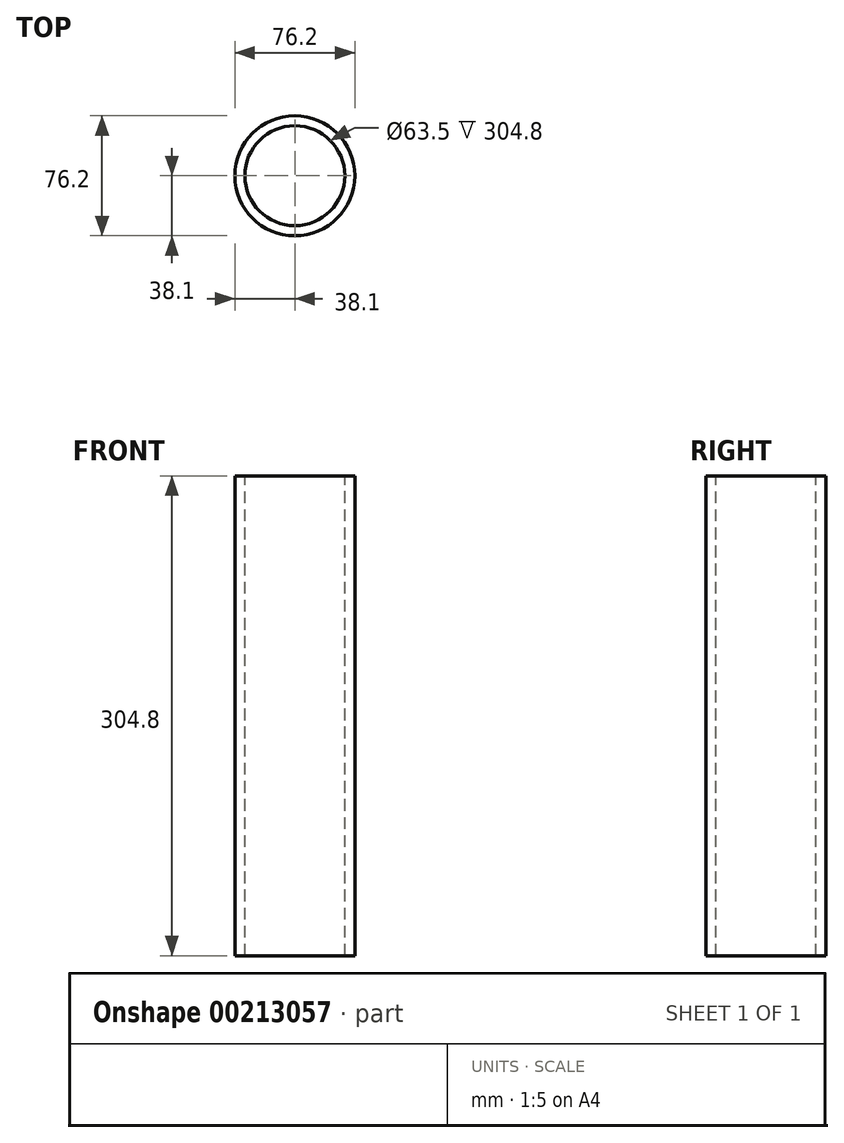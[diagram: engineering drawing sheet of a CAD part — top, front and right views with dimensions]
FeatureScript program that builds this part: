
annotation { "Feature Type Name" : "Feature", "Feature Type Description" : "" }
export const myFeature = defineFeature(function(context is Context, id is Id, definition is map)
    precondition{}
    {
        {
            var Q0;
            Q0=qCreatedBy(makeId("Front.planeOp"),FACE);
            var sketch = newSketch(context, id + "F0", { "sketchPlane" : qUnion([Q0])});
            skLineSegment(sketch, "E0.bottom", {"start": v(-38.1, 152.4) * mm, "end": v(38.1, 152.4) * mm});
            skLineSegment(sketch, "E0.top", {"start": v(-38.1, -152.4) * mm, "end": v(38.1, -152.4) * mm});
            skLineSegment(sketch, "E0.left", {"start": v(-38.1, 152.4) * mm, "end": v(-38.1, -152.4) * mm});
            skLineSegment(sketch, "E0.right", {"start": v(38.1, 152.4) * mm, "end": v(38.1, -152.4) * mm});
            skPoint(sketch, "E0.middle", {"position": v(0, 0) * mm});
            skLineSegment(sketch, "E1.bottom", {"start": v(31.75, 152.4) * mm, "end": v(-31.75, 152.4) * mm});
            skLineSegment(sketch, "E1.top", {"start": v(31.75, -152.4) * mm, "end": v(-31.75, -152.4) * mm});
            skLineSegment(sketch, "E1.left", {"start": v(31.75, 152.4) * mm, "end": v(31.75, -152.4) * mm});
            skLineSegment(sketch, "E1.right", {"start": v(-31.75, 152.4) * mm, "end": v(-31.75, -152.4) * mm});
            skLineSegment(sketch, "E2.top", {"start": v(31.75, -139.7) * mm, "end": v(-31.75, -139.7) * mm});
            skLineSegment(sketch, "E2.left", {"start": v(31.75, -152.4) * mm, "end": v(31.75, -139.7) * mm});
            skLineSegment(sketch, "E2.right", {"start": v(-31.75, -152.4) * mm, "end": v(-31.75, -139.7) * mm});
            skPoint(sketch, "E2.middle", {"position": v(0, -146.05) * mm});
            skLineSegment(sketch, "E3.top", {"start": v(31.75, 139.7) * mm, "end": v(-31.75, 139.7) * mm});
            skLineSegment(sketch, "E3.left", {"start": v(31.75, 152.4) * mm, "end": v(31.75, 139.7) * mm});
            skLineSegment(sketch, "E3.right", {"start": v(-31.75, 152.4) * mm, "end": v(-31.75, 139.7) * mm});
            skPoint(sketch, "E3.middle", {"position": v(0, 146.05) * mm});
            skLineSegment(sketch, "E4.bottom", {"start": v(-12.7, -139.7) * mm, "end": v(12.7, -139.7) * mm});
            skLineSegment(sketch, "E4.top", {"start": v(-12.7, -152.4) * mm, "end": v(12.7, -152.4) * mm});
            skLineSegment(sketch, "E4.left", {"start": v(-12.7, -139.7) * mm, "end": v(-12.7, -152.4) * mm});
            skLineSegment(sketch, "E4.right", {"start": v(12.7, -139.7) * mm, "end": v(12.7, -152.4) * mm});
            skLineSegment(sketch, "E5", {"start": v(0, 152.4) * mm, "end": v(0, -152.4) * mm});
            skSolve(sketch);
        }
        {
            var Q0;
            {var subQ0=sQuery(id+"F0.wireOp",EDGE,"E3.right");Q0=makeQuery(id+"F0.imprint","IMPRINT",FACE,{"disambiguationData":[TD([[makeQuery(id+"F0.imprint","IMPRINT",EDGE,{"derivedFrom":subQ0}),1.0]])]});}
            var Q1;
            {var subQ0=sQuery(id+"F0.wireOp",EDGE,"E0.left");Q1=makeQuery(id+"F0.imprint","IMPRINT",FACE,{"disambiguationData":[TD([[makeQuery(id+"F0.imprint","IMPRINT",EDGE,{"derivedFrom":subQ0}),1.0]])]});}
            var Q2;
            {var subQ0=sQuery(id+"F0.wireOp",EDGE,"E2.right");Q2=makeQuery(id+"F0.imprint","IMPRINT",FACE,{"disambiguationData":[TD([[makeQuery(id+"F0.imprint","IMPRINT",EDGE,{"derivedFrom":subQ0}),-1.0]])]});}
            var Q3;
            Q3=sQuery(id+"F0.wireOp",EDGE,"E5");
            revolve(context, id + "F1", {"entities" : qUnion([Q0, Q1, Q2]), "axis" : qUnion([Q3]), "revolveType" : RevolveType.FULL});
        }
    });
